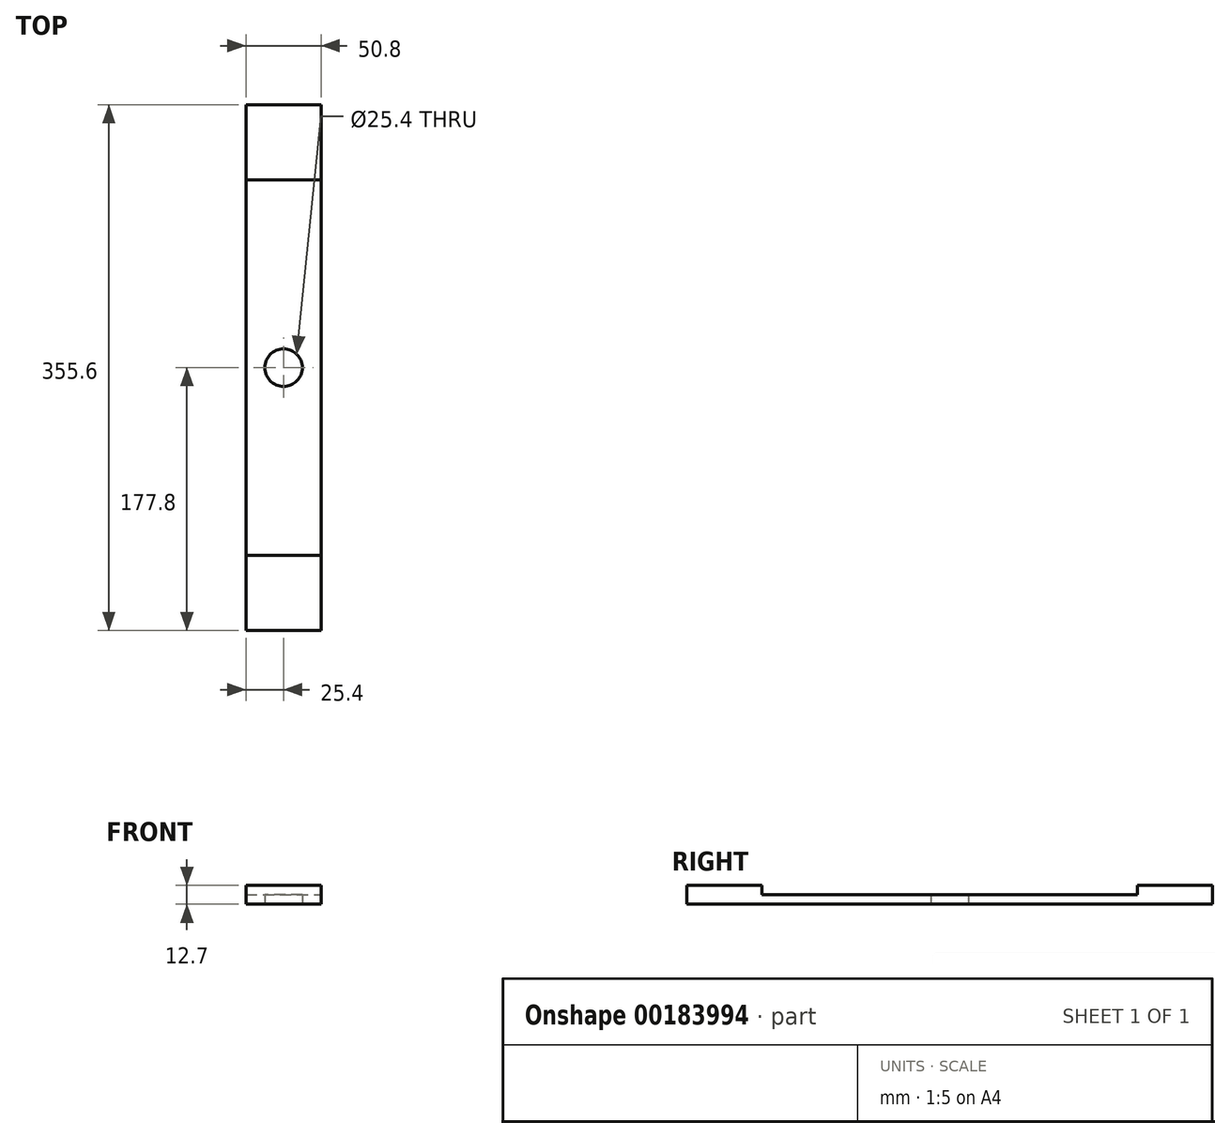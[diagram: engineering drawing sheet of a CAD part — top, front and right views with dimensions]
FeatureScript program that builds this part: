
annotation { "Feature Type Name" : "Feature", "Feature Type Description" : "" }
export const myFeature = defineFeature(function(context is Context, id is Id, definition is map)
    precondition{}
    {
        {
            var Q0;
            Q0=qCreatedBy(makeId("Top.planeOp"),FACE);
            var sketch = newSketch(context, id + "F0", { "sketchPlane" : qUnion([Q0])});
            skLineSegment(sketch, "E0.bottom", {"start": v(25.4, 177.8) * mm, "end": v(-25.4, 177.8) * mm});
            skLineSegment(sketch, "E0.top", {"start": v(25.4, -177.8) * mm, "end": v(-25.4, -177.8) * mm});
            skLineSegment(sketch, "E0.left", {"start": v(25.4, 177.8) * mm, "end": v(25.4, -177.8) * mm});
            skLineSegment(sketch, "E0.right", {"start": v(-25.4, 177.8) * mm, "end": v(-25.4, -177.8) * mm});
            skPoint(sketch, "E0.middle", {"position": v(0, 0) * mm});
            skCircle(sketch, "E1", {"center": v(0, 0) * mm, "radius": 12.7 * mm});
            skSolve(sketch);
        }
        {
            var Q0;
            Q0=makeQuery(id+"F0.imprint","IMPRINT",FACE,{"disambiguationData":[TD([[makeQuery(id+"F0.imprint","IMPRINT",EDGE,{"derivedFrom":sQuery(id+"F0.wireOp",EDGE,"E0.bottom")}),1.0]])]});
            extrude(context, id + "F1", {"entities" : qUnion([Q0]), "depth" : 6.35 * mm});
        }
        {
            var Q0;
            Q0=makeQuery(id+"F1.opExtrude","CAP_FACE",FACE,{"disambiguationData":[OSD([sQuery(id+"F0.wireOp",EDGE,"E0.bottom"),sQuery(id+"F0.wireOp",EDGE,"E0.top"),sQuery(id+"F0.wireOp",EDGE,"E0.left"),sQuery(id+"F0.wireOp",EDGE,"E0.right")])],"isStart":false});
            var sketch = newSketch(context, id + "F2", { "sketchPlane" : qUnion([Q0])});
            skLineSegment(sketch, "E2.bottom", {"start": v(-25.4, -177.8) * mm, "end": v(25.4, -177.8) * mm});
            skLineSegment(sketch, "E2.top", {"start": v(-25.4, -127) * mm, "end": v(25.4, -127) * mm});
            skLineSegment(sketch, "E2.left", {"start": v(-25.4, -177.8) * mm, "end": v(-25.4, -127) * mm});
            skLineSegment(sketch, "E2.right", {"start": v(25.4, -177.8) * mm, "end": v(25.4, -127) * mm});
            skLineSegment(sketch, "E3.bottom", {"start": v(-25.4, 177.8) * mm, "end": v(25.4, 177.8) * mm});
            skLineSegment(sketch, "E3.top", {"start": v(-25.4, 127) * mm, "end": v(25.4, 127) * mm});
            skLineSegment(sketch, "E3.left", {"start": v(-25.4, 177.8) * mm, "end": v(-25.4, 127) * mm});
            skLineSegment(sketch, "E3.right", {"start": v(25.4, 177.8) * mm, "end": v(25.4, 127) * mm});
            skSolve(sketch);
        }
        {
            var Q0;
            Q0 = qSketchRegion(id + "F2", true);
            extrude(context, id + "F3", {"entities" : qUnion([Q0]), "operationType" : NewBodyOperationType.ADD, "depth" : 6.35 * mm});
        }
    });
